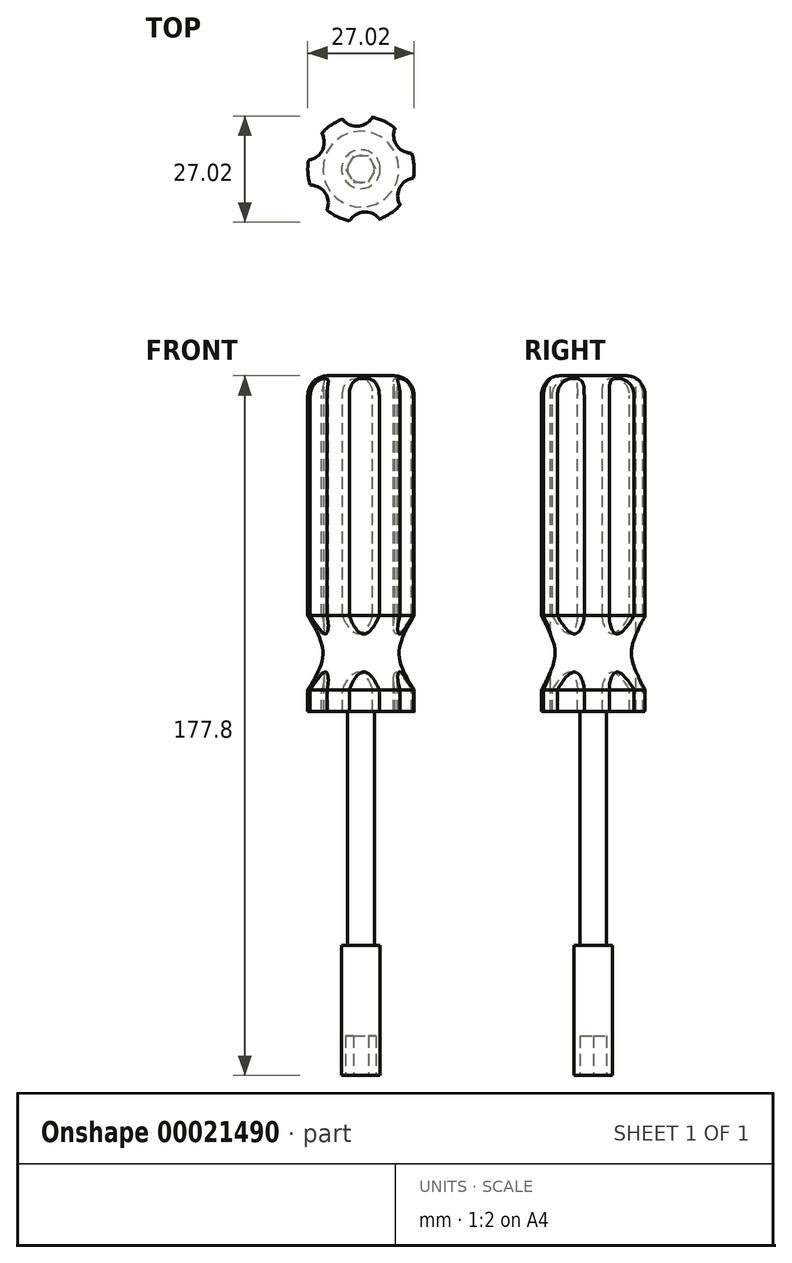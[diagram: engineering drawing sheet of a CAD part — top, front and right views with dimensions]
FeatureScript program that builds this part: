
annotation { "Feature Type Name" : "Feature", "Feature Type Description" : "" }
export const myFeature = defineFeature(function(context is Context, id is Id, definition is map)
    precondition{}
    {
        {
            var Q0;
            Q0=qCreatedBy(makeId("Top.planeOp"),FACE);
            var sketch = newSketch(context, id + "F0", { "sketchPlane" : qUnion([Q0])});
            skCircle(sketch, "E0", {"center": v(0, 0) * mm, "radius": 4.9 * mm});
            skSolve(sketch);
        }
        {
            var Q0;
            Q0 = qSketchRegion(id + "F0", true);
            extrude(context, id + "F1", {"entities" : qUnion([Q0]), "depth" : 33.02 * mm});
        }
        {
            var Q0;
            Q0=makeQuery(id+"F1.opExtrude","CAP_FACE",FACE,{"disambiguationData":[OSD([sQuery(id+"F0.wireOp",EDGE,"E0")])],"isStart":false});
            var sketch = newSketch(context, id + "F2", { "sketchPlane" : qUnion([Q0])});
            skCircle(sketch, "E1", {"center": v(0, 0) * mm, "radius": 3.4 * mm});
            skSolve(sketch);
        }
        {
            var Q0;
            Q0 = qSketchRegion(id + "F2", true);
            extrude(context, id + "F3", {"entities" : qUnion([Q0]), "operationType" : NewBodyOperationType.ADD, "depth" : 59.44 * mm});
        }
        {
            var Q0;
            Q0=makeQuery(id+"F1.opExtrude","CAP_FACE",FACE,{"disambiguationData":[OSD([sQuery(id+"F0.wireOp",EDGE,"E0")])],"isStart":true});
            var sketch = newSketch(context, id + "F4", { "sketchPlane" : qUnion([Q0])});
            skCircle(sketch, "E2.cCircle", {"center": v(0, 0) * mm, "radius": 3.35 * mm, "construction": true});
            skLineSegment(sketch, "E2.0", {"start": v(3.87, 0) * mm, "end": v(1.94, -3.35) * mm});
            skLineSegment(sketch, "E2.1", {"start": v(1.94, -3.35) * mm, "end": v(-1.94, -3.35) * mm});
            skLineSegment(sketch, "E2.2", {"start": v(-1.94, -3.35) * mm, "end": v(-3.87, 0) * mm});
            skLineSegment(sketch, "E2.3", {"start": v(-3.87, 0) * mm, "end": v(-1.94, 3.35) * mm});
            skLineSegment(sketch, "E2.4", {"start": v(-1.94, 3.35) * mm, "end": v(1.94, 3.35) * mm});
            skLineSegment(sketch, "E2.5", {"start": v(1.94, 3.35) * mm, "end": v(3.87, 0) * mm});
            skPoint(sketch, "E2.0.midPoint", {"position": v(2.9, -1.68) * mm});
            skSolve(sketch);
        }
        {
            var Q0;
            Q0 = qSketchRegion(id + "F4", true);
            extrude(context, id + "F5", {"entities" : qUnion([Q0]), "operationType" : NewBodyOperationType.REMOVE, "oppositeDirection" : true, "depth" : 10.06 * mm});
        }
        {
            var Q0;
            Q0=makeQuery(id+"F3.opExtrude","CAP_FACE",FACE,{"disambiguationData":[OSD([sQuery(id+"F2.wireOp",EDGE,"E1")])],"isStart":false});
            var sketch = newSketch(context, id + "F6", { "sketchPlane" : qUnion([Q0])});
            skCircle(sketch, "E3", {"center": v(0, 0) * mm, "radius": 13.51 * mm});
            skSolve(sketch);
        }
        {
            var Q0;
            Q0 = qSketchRegion(id + "F6", true);
            extrude(context, id + "F7", {"entities" : qUnion([Q0]), "operationType" : NewBodyOperationType.ADD, "depth" : 5.54 * mm});
        }
        {
            var Q0;
            Q0=makeQuery(id+"F7.opExtrude","CAP_FACE",FACE,{"disambiguationData":[OSD([sQuery(id+"F6.wireOp",EDGE,"E3")])],"isStart":true});
            cPlane(context, id + "F8", {"entities" : qUnion([Q0]), "cplaneType" : CPlaneType.OFFSET, "offset" : 14.76 * mm, "oppositeDirection" : true, "width" : 152.4 * mm, "height" : 152.4 * mm});
        }
        {
            var Q0;
            Q0=qCreatedBy(id+"F8.planeOp",FACE);
            var sketch = newSketch(context, id + "F9", { "sketchPlane" : qUnion([Q0])});
            skCircle(sketch, "E4", {"center": v(0, 0) * mm, "radius": 9.68 * mm});
            skSolve(sketch);
        }
        {
            var Q0;
            Q0=makeQuery(id+"F7.opExtrude","CAP_FACE",FACE,{"disambiguationData":[OSD([sQuery(id+"F6.wireOp",EDGE,"E3")])],"isStart":true});
            cPlane(context, id + "F10", {"entities" : qUnion([Q0]), "cplaneType" : CPlaneType.OFFSET, "offset" : 24.38 * mm, "oppositeDirection" : true, "width" : 152.4 * mm, "height" : 152.4 * mm});
        }
        {
            var Q0;
            Q0=qCreatedBy(id+"F10.planeOp",FACE);
            var sketch = newSketch(context, id + "F11", { "sketchPlane" : qUnion([Q0])});
            skCircle(sketch, "E5.0", {"center": v(0, 0) * mm, "radius": 13.51 * mm});
            skSolve(sketch);
        }
        {
            var Q0;
            Q0=makeQuery(id+"F11.imprint","IMPRINT",FACE,{"disambiguationData":[TD([[makeQuery(id+"F11.imprint","IMPRINT",EDGE,{"derivedFrom":sQuery(id+"F11.wireOp",EDGE,"E5.0")}),1.0]])]});
            var Q1;
            Q1=makeQuery(id+"F9.imprint","IMPRINT",FACE,{"disambiguationData":[TD([[makeQuery(id+"F9.imprint","IMPRINT",EDGE,{"derivedFrom":sQuery(id+"F9.wireOp",EDGE,"E4")}),1.0]])]});
            var Q2;
            Q2=makeQuery(id+"F7.opExtrude","CAP_FACE",FACE,{"disambiguationData":[OSD([sQuery(id+"F6.wireOp",EDGE,"E3")])],"isStart":false});
            loft(context, id + "F12", {"sheetProfilesArray" : [{ "sheetProfileEntities" : qUnion([Q0]) }, { "sheetProfileEntities" : qUnion([Q1]) }, { "sheetProfileEntities" : qUnion([Q2]) }]});
        }
        {
            var Q0;
            Q0 = qSketchRegion(id + "F11", true);
            extrude(context, id + "F13", {"entities" : qUnion([Q0]), "oppositeDirection" : true, "depth" : 60.96 * mm});
        }
        {
            var Q0;
            Q0=makeQuery(id+"F13.opExtrude","CAP_EDGE",EDGE,{"disambiguationData":[OSD([sQuery(id+"F11.wireOp",EDGE,"E5.0")])],"isStart":false});
            fillet(context, id + "F14", {"entities" : qUnion([Q0]), "radius" : 5.08 * mm, "tangentPropagation" : true, "allowEdgeOverflow" : false});
        }
        {
            var Q0;
            Q0=makeQuery(id+"F13.opExtrude","CAP_FACE",FACE,{"disambiguationData":[OSD([sQuery(id+"F11.wireOp",EDGE,"E5.0")])],"isStart":false});
            var sketch = newSketch(context, id + "F15", { "sketchPlane" : qUnion([Q0])});
            skArc(sketch, "E6", {"start": v(-4.67, 12.68) * mm, "mid": v(-0.73, 10.9) * mm, "end": v(2.93, 13.2) * mm});
            skArc(sketch, "E7", {"start": v(2.93, 13.2) * mm, "mid": v(-0.9, 13.48) * mm, "end": v(-4.67, 12.68) * mm});
            skArc(sketch, "E8.1.0", {"start": v(-13.32, 2.3) * mm, "mid": v(-9.8, 4.82) * mm, "end": v(-9.96, 9.14) * mm});
            skArc(sketch, "E8.1.1", {"start": v(-9.96, 9.14) * mm, "mid": v(-12.13, 5.96) * mm, "end": v(-13.32, 2.3) * mm});
            skArc(sketch, "E8.2.0", {"start": v(-8.65, -10.38) * mm, "mid": v(-9.07, -6.08) * mm, "end": v(-12.9, -4.05) * mm});
            skArc(sketch, "E8.2.1", {"start": v(-12.9, -4.05) * mm, "mid": v(-11.22, -7.52) * mm, "end": v(-8.65, -10.38) * mm});
            skArc(sketch, "E8.3.0", {"start": v(4.67, -12.68) * mm, "mid": v(0.73, -10.9) * mm, "end": v(-2.93, -13.2) * mm});
            skArc(sketch, "E8.3.1", {"start": v(-2.93, -13.2) * mm, "mid": v(0.9, -13.48) * mm, "end": v(4.67, -12.68) * mm});
            skArc(sketch, "E8.4.0", {"start": v(13.32, -2.3) * mm, "mid": v(9.8, -4.82) * mm, "end": v(9.96, -9.14) * mm});
            skArc(sketch, "E8.4.1", {"start": v(9.96, -9.14) * mm, "mid": v(12.13, -5.96) * mm, "end": v(13.32, -2.3) * mm});
            skArc(sketch, "E8.5.0", {"start": v(8.65, 10.38) * mm, "mid": v(9.07, 6.08) * mm, "end": v(12.9, 4.05) * mm});
            skArc(sketch, "E8.5.1", {"start": v(12.9, 4.05) * mm, "mid": v(11.22, 7.52) * mm, "end": v(8.65, 10.38) * mm});
            skSolve(sketch);
        }
        {
            var Q0;
            Q0 = qSketchRegion(id + "F15", true);
            extrude(context, id + "F16", {"entities" : qUnion([Q0]), "operationType" : NewBodyOperationType.REMOVE, "endBound" : BoundingType.THROUGH_ALL, "oppositeDirection" : true, "depth" : 25.4 * mm});
        }
    });
